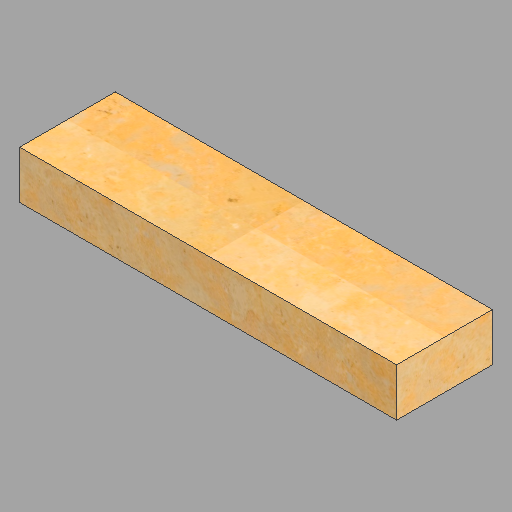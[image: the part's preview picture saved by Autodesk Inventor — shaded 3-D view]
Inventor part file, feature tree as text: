
AUTODESK INVENTOR PART (.ipt)
format: ipt  version: 2023 (Build 270158030, 158C)  size: 243,712 bytes
history: native  units: in
note: dims shown in document units (in); Inventor stores cm internally (conversion verified against a paired STEP export)
features: extrude x1, sketch x1
ambient origin geometry x8: Origin, YZ Plane, XZ Plane, XY Plane, X Axis, Y Axis, Z Axis, Center Point
bodies: Solid1 (feature_tree)
feature tree (2):
  extrude  "Extrusion1"  Depth=6.0in
  sketch  "Sketch1"  dims[d0=23.625in d1=6.0in d2=3.0in d3=0.0in]
